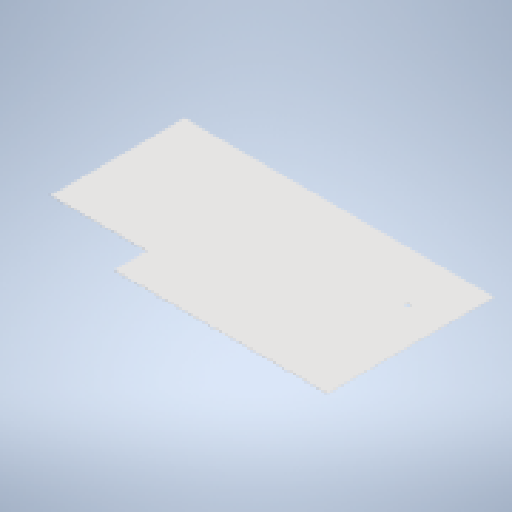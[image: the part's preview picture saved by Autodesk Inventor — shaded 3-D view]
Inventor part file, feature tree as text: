
AUTODESK INVENTOR PART (.ipt)
format: ipt  version: 2025 (Build 290162010, 162A)  size: 241,152 bytes
history: native  units: mm
features: other x3, sketch x3, sheet_metal_op x1, extrude x1
ambient origin geometry x8: Origin, YZ Plane, XZ Plane, XY Plane, X Axis, Y Axis, Z Axis, Center Point
bodies: Solid1 (feature_tree)
feature tree (8):
  sheet_metal_op  "Face1"
  other  "Mark1"
  extrude  "Extrusion2"  Depth=1480.0mm
  sketch  "Sketch1"  dims[d0=2748.0mm d1=1480.0mm]
  other  "Plate1"
  sketch  "Sketch5"  dims[d2=3.0mm]
  sketch  "Sketch6"  dims[d26=200.0mm d27=15.0mm d28=25.0mm d29=25.0mm d30=293.0mm d31=853.0mm d32=40.0mm d33=320.0mm d34=450.0mm d35=10.0mm d36=0.0mm]
  other  "Definition1"
